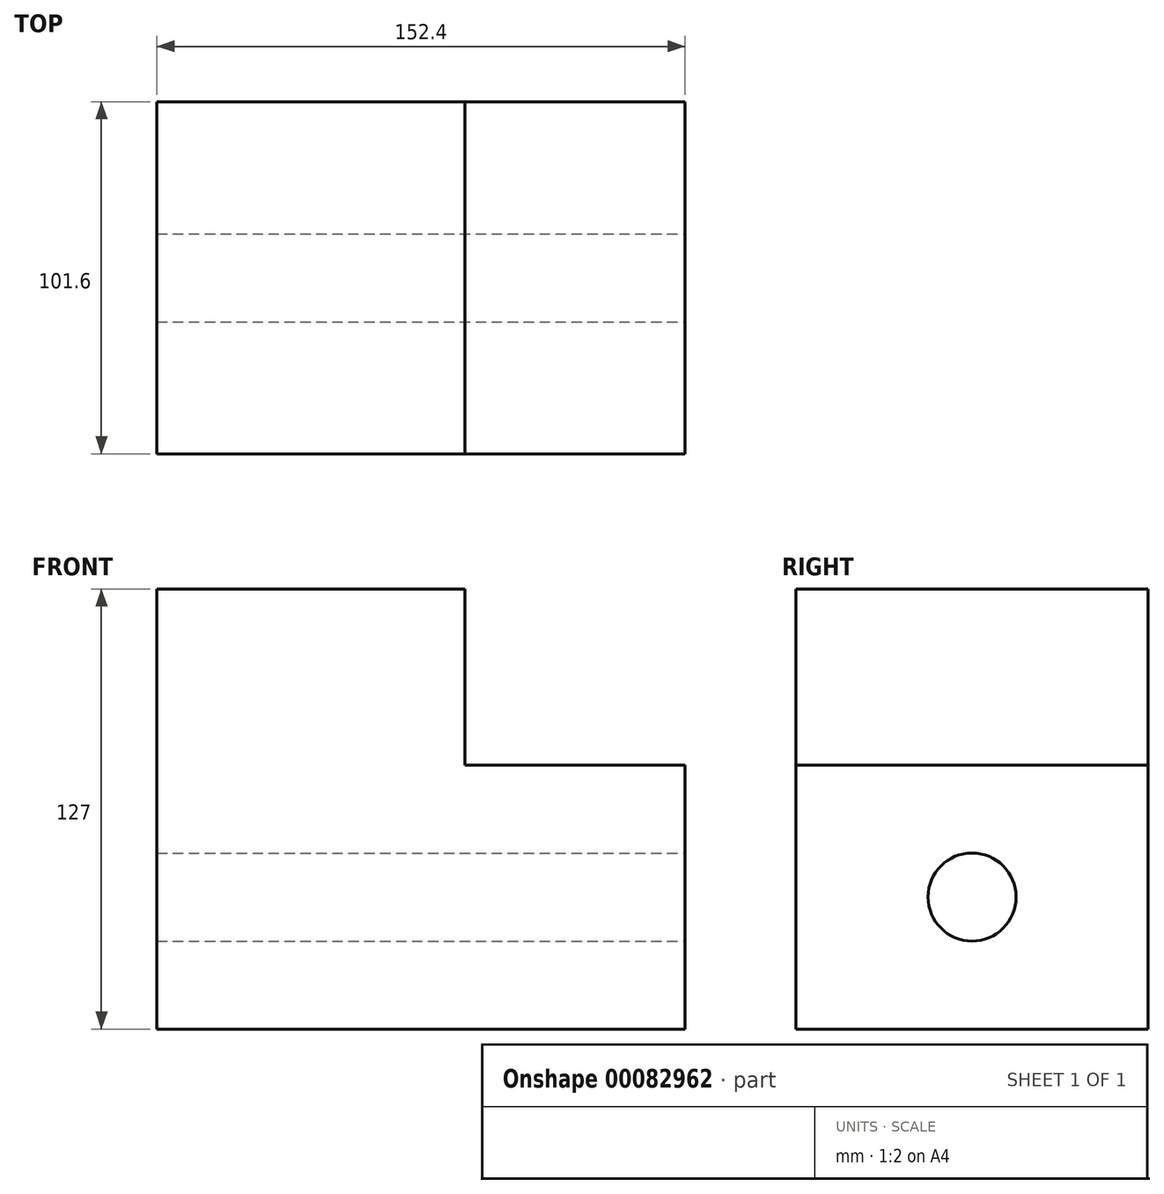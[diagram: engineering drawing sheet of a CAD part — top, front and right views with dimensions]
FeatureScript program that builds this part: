
annotation { "Feature Type Name" : "Feature", "Feature Type Description" : "" }
export const myFeature = defineFeature(function(context is Context, id is Id, definition is map)
    precondition{}
    {
        {
            var Q0;
            Q0=qCreatedBy(makeId("Top.planeOp"),FACE);
            var sketch = newSketch(context, id + "F0", { "sketchPlane" : qUnion([Q0])});
            skLineSegment(sketch, "E0.bottom", {"start": v(0, 0) * mm, "end": v(152.4, 0) * mm});
            skLineSegment(sketch, "E0.top", {"start": v(0, 101.6) * mm, "end": v(152.4, 101.6) * mm});
            skLineSegment(sketch, "E0.left", {"start": v(0, 0) * mm, "end": v(0, 101.6) * mm});
            skLineSegment(sketch, "E0.right", {"start": v(152.4, 0) * mm, "end": v(152.4, 101.6) * mm});
            skSolve(sketch);
        }
        {
            var Q0;
            Q0=makeQuery(id+"F0.imprint","IMPRINT",FACE,{"disambiguationData":[TD([[makeQuery(id+"F0.imprint","IMPRINT",EDGE,{"derivedFrom":sQuery(id+"F0.wireOp",EDGE,"E0.bottom")}),1.0]])]});
            extrude(context, id + "F1", {"entities" : qUnion([Q0]), "depth" : 127 * mm});
        }
        {
            var Q0;
            Q0=makeQuery(id+"F1.opExtrude","SWEPT_FACE",FACE,{"disambiguationData":[OSD([sQuery(id+"F0.wireOp",EDGE,"E0.bottom")])]});
            var sketch = newSketch(context, id + "F2", { "sketchPlane" : qUnion([Q0])});
            skLineSegment(sketch, "E1.bottom", {"start": v(152.4, 127) * mm, "end": v(88.9, 127) * mm});
            skLineSegment(sketch, "E1.top", {"start": v(152.4, 76.2) * mm, "end": v(88.9, 76.2) * mm});
            skLineSegment(sketch, "E1.left", {"start": v(152.4, 127) * mm, "end": v(152.4, 76.2) * mm});
            skLineSegment(sketch, "E1.right", {"start": v(88.9, 127) * mm, "end": v(88.9, 76.2) * mm});
            skSolve(sketch);
        }
        {
            var Q0;
            Q0=makeQuery(id+"F2.imprint","IMPRINT",FACE,{"disambiguationData":[TD([[makeQuery(id+"F2.imprint","IMPRINT",EDGE,{"derivedFrom":sQuery(id+"F2.wireOp",EDGE,"E1.bottom")}),-1.0]])]});
            extrude(context, id + "F3", {"entities" : qUnion([Q0]), "operationType" : NewBodyOperationType.ADD, "oppositeDirection" : true, "depth" : 101.6 * mm});
        }
        {
            var Q0;
            Q0=makeQuery(id+"F1.opExtrude","SWEPT_FACE",FACE,{"disambiguationData":[OSD([sQuery(id+"F0.wireOp",EDGE,"E0.bottom")])]});
            var sketch = newSketch(context, id + "F4", { "sketchPlane" : qUnion([Q0])});
            skLineSegment(sketch, "E2.bottom", {"start": v(152.4, 127) * mm, "end": v(88.9, 127) * mm});
            skLineSegment(sketch, "E2.top", {"start": v(152.4, 76.2) * mm, "end": v(88.9, 76.2) * mm});
            skLineSegment(sketch, "E2.left", {"start": v(152.4, 127) * mm, "end": v(152.4, 76.2) * mm});
            skLineSegment(sketch, "E2.right", {"start": v(88.9, 127) * mm, "end": v(88.9, 76.2) * mm});
            skSolve(sketch);
        }
        {
            var Q0;
            Q0=makeQuery(id+"F4.imprint","IMPRINT",FACE,{"disambiguationData":[TD([[makeQuery(id+"F4.imprint","IMPRINT",EDGE,{"derivedFrom":sQuery(id+"F4.wireOp",EDGE,"E2.bottom")}),-1.0]])]});
            extrude(context, id + "F5", {"entities" : qUnion([Q0]), "operationType" : NewBodyOperationType.REMOVE, "oppositeDirection" : true, "depth" : 101.6 * mm});
        }
        {
            var Q0;
            Q0=makeQuery(id+"F1.opExtrude","SWEPT_FACE",FACE,{"disambiguationData":[OSD([sQuery(id+"F0.wireOp",EDGE,"E0.right")])]});
            var sketch = newSketch(context, id + "F6", { "sketchPlane" : qUnion([Q0])});
            skLineSegment(sketch, "E3.bottom", {"start": v(0, 0) * mm, "end": v(50.8, 0) * mm});
            skLineSegment(sketch, "E3.top", {"start": v(0, 38.1) * mm, "end": v(50.8, 38.1) * mm});
            skLineSegment(sketch, "E3.left", {"start": v(0, 0) * mm, "end": v(0, 38.1) * mm});
            skLineSegment(sketch, "E3.right", {"start": v(50.8, 0) * mm, "end": v(50.8, 38.1) * mm});
            skPoint(sketch, "E4", {"position": v(50.8, 38.1) * mm});
            skCircle(sketch, "E5", {"center": v(50.8, 38.1) * mm, "radius": 12.7 * mm});
            skSolve(sketch);
        }
        {
            var Q0;
            Q0=sQuery(id+"F6.wireOp",VERTEX,"E4");
            var Q1;
            Q1=makeQuery(id+"F1.opExtrude","SWEPT_BODY",BODY,{"disambiguationData":[OSD([sQuery(id+"F0.wireOp",EDGE,"E0.bottom"),sQuery(id+"F0.wireOp",EDGE,"E0.top"),sQuery(id+"F0.wireOp",EDGE,"E0.left"),sQuery(id+"F0.wireOp",EDGE,"E0.right")])]});
            hole(context, id + "F7", {"style" : HoleStyle.SIMPLE, "endStyle" : HoleEndStyle.THROUGH, "holeDiameter" : 25.4 * mm, "locations" : qUnion([Q0]), "scope" : qUnion([Q1]), "isTappedThrough" : true});
        }
    });
